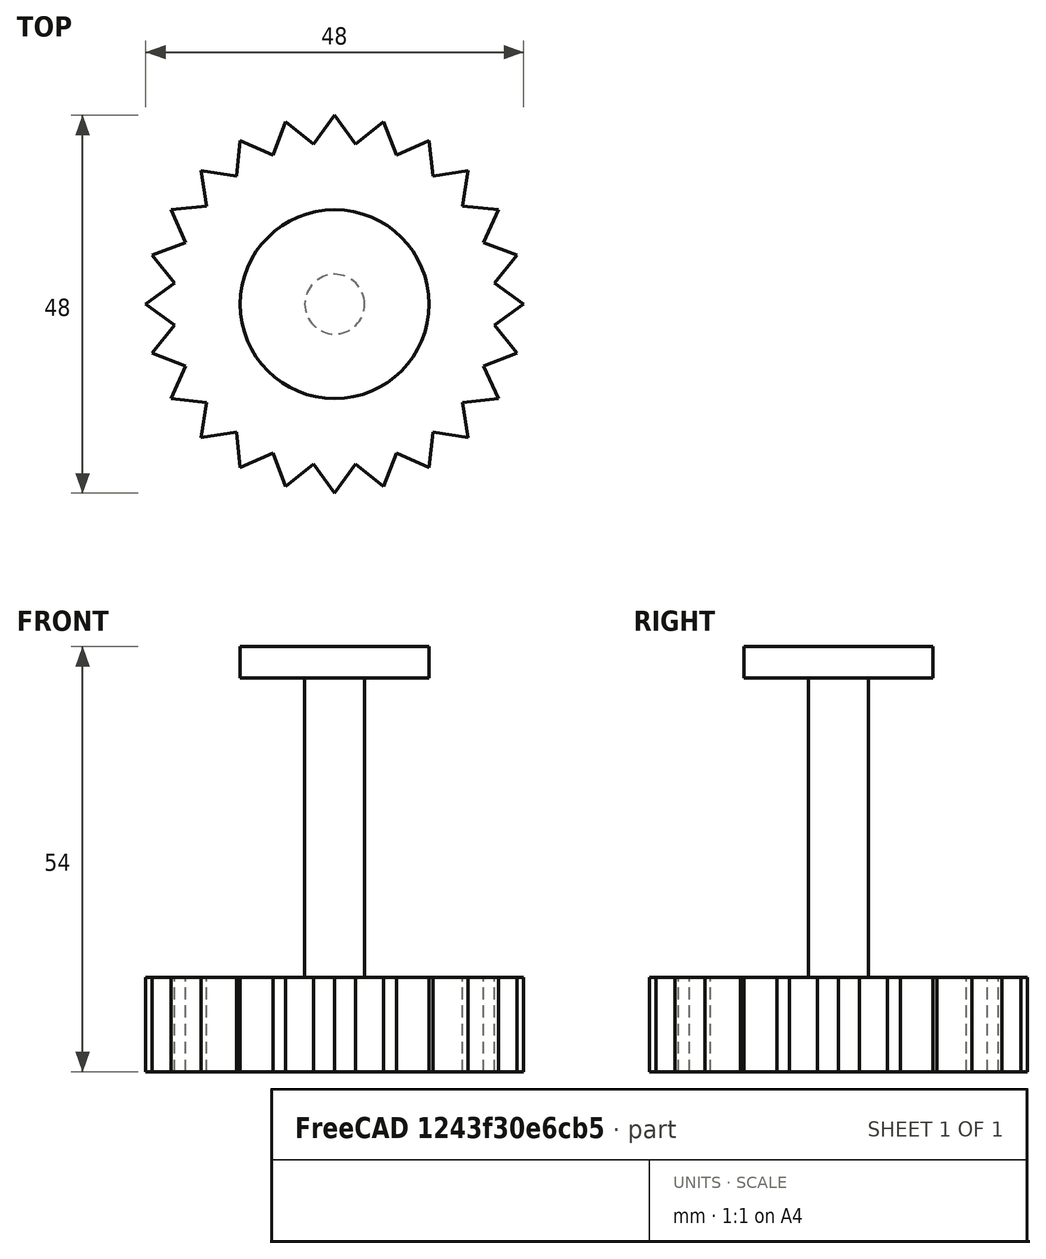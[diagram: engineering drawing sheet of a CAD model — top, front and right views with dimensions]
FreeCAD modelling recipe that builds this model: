
FCSTD DOCUMENT  (FreeCAD 1.2R20251230 (Git shallow))
Label: vanity_cable_clamp_knob_screw
License: Creative Commons Attribution 4.0
LicenseURL: https://creativecommons.org/licenses/by/4.0/
objects: Sketcher::SketchObject×3, PartDesign::Pad×3, App::Point×1, PartDesign::Body×1
note: 16 computed .brp shape members not serialized (recipe doc carries the construction recipe); baked Part::Feature solids carry a one-line shape summary decoded from their .brp

FEATURE [App::Point] Origin001
  Role = Origin
FEATURE [Sketcher::SketchObject] Sketch_01_GearLike_Knob_Profile
  ArcFitTolerance = 1e-06
  ExternalTypes = [0]
  FullyConstrained = false
  MakeInternals = false
  sketch-geometry (48):
    g0: LineSegment StartX=24 StartY=0 StartZ=0 EndX=20.3246 EndY=2.67579 EndZ=0
    g1: LineSegment StartX=20.3246 StartY=2.67579 StartZ=0 EndX=23.1822 EndY=6.21166 EndZ=0
    g2: LineSegment StartX=23.1822 StartY=6.21166 StartZ=0 EndX=18.9395 EndY=7.84501 EndZ=0
    g3: LineSegment StartX=18.9395 StartY=7.84501 StartZ=0 EndX=20.7846 EndY=12 EndZ=0
    g4: LineSegment StartX=20.7846 StartY=12 StartZ=0 EndX=16.2637 EndY=12.4796 EndZ=0
    g5: LineSegment StartX=16.2637 StartY=12.4796 StartZ=0 EndX=16.9706 EndY=16.9706 EndZ=0
    g6: LineSegment StartX=16.9706 StartY=16.9706 StartZ=0 EndX=12.4796 EndY=16.2637 EndZ=0
    g7: LineSegment StartX=12.4796 StartY=16.2637 StartZ=0 EndX=12 EndY=20.7846 EndZ=0
    g8: LineSegment StartX=12 StartY=20.7846 StartZ=0 EndX=7.84501 EndY=18.9395 EndZ=0
    g9: LineSegment StartX=7.84501 StartY=18.9395 StartZ=0 EndX=6.21166 EndY=23.1822 EndZ=0
    g10: LineSegment StartX=6.21166 StartY=23.1822 StartZ=0 EndX=2.67579 EndY=20.3246 EndZ=0
    g11: LineSegment StartX=2.67579 StartY=20.3246 StartZ=0 EndX=1.3e-15 EndY=24 EndZ=0
    g12: LineSegment StartX=1.3e-15 StartY=24 StartZ=0 EndX=-2.67579 EndY=20.3246 EndZ=0
    g13: LineSegment StartX=-2.67579 StartY=20.3246 StartZ=0 EndX=-6.21166 EndY=23.1822 EndZ=0
    g14: LineSegment StartX=-6.21166 StartY=23.1822 StartZ=0 EndX=-7.84501 EndY=18.9395 EndZ=0
    g15: LineSegment StartX=-7.84501 StartY=18.9395 StartZ=0 EndX=-12 EndY=20.7846 EndZ=0
    g16: LineSegment StartX=-12 StartY=20.7846 StartZ=0 EndX=-12.4796 EndY=16.2637 EndZ=0
    g17: LineSegment StartX=-12.4796 StartY=16.2637 StartZ=0 EndX=-16.9706 EndY=16.9706 EndZ=0
    g18: LineSegment StartX=-16.9706 StartY=16.9706 StartZ=0 EndX=-16.2637 EndY=12.4796 EndZ=0
    g19: LineSegment StartX=-16.2637 StartY=12.4796 StartZ=0 EndX=-20.7846 EndY=12 EndZ=0
    g20: LineSegment StartX=-20.7846 StartY=12 StartZ=0 EndX=-18.9395 EndY=7.84501 EndZ=0
    g21: LineSegment StartX=-18.9395 StartY=7.84501 StartZ=0 EndX=-23.1822 EndY=6.21166 EndZ=0
    g22: LineSegment StartX=-23.1822 StartY=6.21166 StartZ=0 EndX=-20.3246 EndY=2.67579 EndZ=0
    g23: LineSegment StartX=-20.3246 StartY=2.67579 StartZ=0 EndX=-24 EndY=3.1e-15 EndZ=0
    g24: LineSegment StartX=-24 StartY=3.1e-15 StartZ=0 EndX=-20.3246 EndY=-2.67579 EndZ=0
    g25: LineSegment StartX=-20.3246 StartY=-2.67579 StartZ=0 EndX=-23.1822 EndY=-6.21166 EndZ=0
    g26: LineSegment StartX=-23.1822 StartY=-6.21166 StartZ=0 EndX=-18.9395 EndY=-7.84501 EndZ=0
    g27: LineSegment StartX=-18.9395 StartY=-7.84501 StartZ=0 EndX=-20.7846 EndY=-12 EndZ=0
    g28: LineSegment StartX=-20.7846 StartY=-12 StartZ=0 EndX=-16.2637 EndY=-12.4796 EndZ=0
    g29: LineSegment StartX=-16.2637 StartY=-12.4796 StartZ=0 EndX=-16.9706 EndY=-16.9706 EndZ=0
    g30: LineSegment StartX=-16.9706 StartY=-16.9706 StartZ=0 EndX=-12.4796 EndY=-16.2637 EndZ=0
    g31: LineSegment StartX=-12.4796 StartY=-16.2637 StartZ=0 EndX=-12 EndY=-20.7846 EndZ=0
    g32: LineSegment StartX=-12 StartY=-20.7846 StartZ=0 EndX=-7.84501 EndY=-18.9395 EndZ=0
    g33: LineSegment StartX=-7.84501 StartY=-18.9395 StartZ=0 EndX=-6.21166 EndY=-23.1822 EndZ=0
    g34: LineSegment StartX=-6.21166 StartY=-23.1822 StartZ=0 EndX=-2.67579 EndY=-20.3246 EndZ=0
    g35: LineSegment StartX=-2.67579 StartY=-20.3246 StartZ=0 EndX=-4.4e-15 EndY=-24 EndZ=0
    g36: LineSegment StartX=-4.4e-15 StartY=-24 StartZ=0 EndX=2.67579 EndY=-20.3246 EndZ=0
    g37: LineSegment StartX=2.67579 StartY=-20.3246 StartZ=0 EndX=6.21166 EndY=-23.1822 EndZ=0
    g38: LineSegment StartX=6.21166 StartY=-23.1822 StartZ=0 EndX=7.84501 EndY=-18.9395 EndZ=0
    g39: LineSegment StartX=7.84501 StartY=-18.9395 StartZ=0 EndX=12 EndY=-20.7846 EndZ=0
    g40: LineSegment StartX=12 StartY=-20.7846 StartZ=0 EndX=12.4796 EndY=-16.2637 EndZ=0
    g41: LineSegment StartX=12.4796 StartY=-16.2637 StartZ=0 EndX=16.9706 EndY=-16.9706 EndZ=0
    g42: LineSegment StartX=16.9706 StartY=-16.9706 StartZ=0 EndX=16.2637 EndY=-12.4796 EndZ=0
    g43: LineSegment StartX=16.2637 StartY=-12.4796 StartZ=0 EndX=20.7846 EndY=-12 EndZ=0
    g44: LineSegment StartX=20.7846 StartY=-12 StartZ=0 EndX=18.9395 EndY=-7.84501 EndZ=0
    g45: LineSegment StartX=18.9395 StartY=-7.84501 StartZ=0 EndX=23.1822 EndY=-6.21166 EndZ=0
    g46: LineSegment StartX=23.1822 StartY=-6.21166 StartZ=0 EndX=20.3246 EndY=-2.67579 EndZ=0
    g47: LineSegment StartX=20.3246 StartY=-2.67579 StartZ=0 EndX=24 EndY=0 EndZ=0
  constraints (48):
    c: Coincident(g0,g1)
    c: Coincident(g1,g2)
    c: Coincident(g2,g3)
    c: Coincident(g3,g4)
    c: Coincident(g4,g5)
    c: Coincident(g5,g6)
    c: Coincident(g6,g7)
    c: Coincident(g7,g8)
    c: Coincident(g8,g9)
    c: Coincident(g9,g10)
    c: Coincident(g10,g11)
    c: Coincident(g11,g12)
    c: Coincident(g12,g13)
    c: Coincident(g13,g14)
    c: Coincident(g14,g15)
    c: Coincident(g15,g16)
    c: Coincident(g16,g17)
    c: Coincident(g17,g18)
    c: Coincident(g18,g19)
    c: Coincident(g19,g20)
    c: Coincident(g20,g21)
    c: Coincident(g21,g22)
    c: Coincident(g22,g23)
    c: Coincident(g23,g24)
    c: Coincident(g24,g25)
    c: Coincident(g25,g26)
    c: Coincident(g26,g27)
    c: Coincident(g27,g28)
    c: Coincident(g28,g29)
    c: Coincident(g29,g30)
    c: Coincident(g30,g31)
    c: Coincident(g31,g32)
    c: Coincident(g32,g33)
    c: Coincident(g33,g34)
    c: Coincident(g34,g35)
    c: Coincident(g35,g36)
    c: Coincident(g36,g37)
    c: Coincident(g37,g38)
    c: Coincident(g38,g39)
    c: Coincident(g39,g40)
    c: Coincident(g40,g41)
    c: Coincident(g41,g42)
    c: Coincident(g42,g43)
    c: Coincident(g43,g44)
    c: Coincident(g44,g45)
    c: Coincident(g45,g46)
    c: Coincident(g46,g47)
    c: Coincident(g47,g0)
FEATURE [PartDesign::Pad] Pad_02_GearLike_Knob
  Direction = (0,0,1)
  Length = 12
  Length2 = 10
  Profile = -> Sketch_01_GearLike_Knob_Profile
  Refine = true
  SideType = 0
  Suppressed = false
  Type = 0
  Type2 = 0
FEATURE [Sketcher::SketchObject] Sketch_03_Screw_Shaft_Profile
  ArcFitTolerance = 1e-06
  ExternalTypes = [0]
  FullyConstrained = false
  MakeInternals = false
  Placement = pos=(0,0,12) rot=(0,0,1;0rad)
  sketch-geometry (1):
    g0: Circle CenterX=0 CenterY=0 CenterZ=0 NormalX=0 NormalY=0 NormalZ=1 AngleXU=0 Radius=3.8
  constraints (1):
    c: Radius(g0) = 3.8
FEATURE [PartDesign::Pad] Pad_04_Screw_Shaft
  BaseFeature = -> Pad_02_GearLike_Knob
  Direction = (0,0,1)
  Length = 38
  Length2 = 10
  Profile = -> Sketch_03_Screw_Shaft_Profile
  Refine = true
  SideType = 0
  Suppressed = false
  Type = 0
  Type2 = 0
FEATURE [Sketcher::SketchObject] Sketch_05_Pressure_Pad_Profile
  ArcFitTolerance = 1e-06
  ExternalTypes = [0]
  FullyConstrained = false
  MakeInternals = false
  Placement = pos=(0,0,50) rot=(0,0,1;0rad)
  sketch-geometry (1):
    g0: Circle CenterX=0 CenterY=0 CenterZ=0 NormalX=0 NormalY=0 NormalZ=1 AngleXU=0 Radius=12
  constraints (1):
    c: Radius(g0) = 12
FEATURE [PartDesign::Pad] Pad_06_Pressure_Pad
  BaseFeature = -> Pad_04_Screw_Shaft
  Direction = (0,0,1)
  Length = 4
  Length2 = 10
  Profile = -> Sketch_05_Pressure_Pad_Profile
  Refine = true
  SideType = 0
  Suppressed = false
  Type = 0
  Type2 = 0
FEATURE [PartDesign::Body] Body_KnurledKnobScrew
  AllowCompound = true
  Group = -> [Sketch_01_GearLike_Knob_Profile,Pad_02_GearLike_Knob,Sketch_03_Screw_Shaft_Profile,Pad_04_Screw_Shaft,Sketch_05_Pressure_Pad_Profile,Pad_06_Pressure_Pad]
  Origin = -> Origin
  Tip = -> Pad_06_Pressure_Pad
